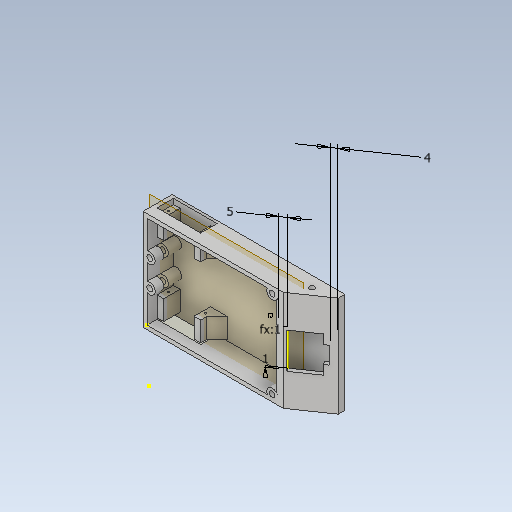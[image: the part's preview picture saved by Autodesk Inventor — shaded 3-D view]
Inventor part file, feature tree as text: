
AUTODESK INVENTOR PART (.ipt)
format: ipt  version: 2020 (Build 240168000, 168)  size: 331,776 bytes
history: native  units: mm
features: extrude x16, sketch x14, reference x11, other x8, projected_geometry x6, plane x2, hole x1, chamfer x1
ambient origin geometry x8: Origin, YZ Plane, XZ Plane, XY Plane, X Axis, Y Axis, Z Axis, Center Point
bodies: Solid1 (feature_tree)
feature tree (59):
  sketch  "Sketch1"  dims[d0=100.0mm d1=70.0mm]
  extrude  "Extrusion1"  Depth=70.0mm
  extrude  "Extrusion2"  Depth=2.0mm TaperAngle=0.0deg
  extrude  "Extrusion3"  Depth=33.0mm
  sketch  "Sketch3"  dims[d5=20.0mm d6=0.0mm d7=33.0mm]
  plane  "Work Plane1"
  extrude  "Extrusion4"  Depth=12.4mm TaperAngle=0.0deg
  hole  "Hole1"  [1 undecoded]
  sketch  "Sketch5"  dims[d11=15.0mm d12=15.0mm]
  extrude  "Extrusion5"  Depth=15.0mm
  extrude  "Extrusion6"  Depth=8.0mm
  extrude  "Extrusion7"  Depth=5.0mm TaperAngle=0.0deg
  extrude  "Extrusion8"  Depth=76.0mm TaperAngle=0.0deg
  extrude  "Extrusion9"  Depth=3.0mm TaperAngle=0.0deg
  extrude  "Extrusion10"  Depth=27.0mm
  sketch  "Sketch9"  dims[d33=5.0mm d40=41.25mm d41=0.0mm]
  sketch  "Sketch10"  dims[d42=3.0mm d43=76.0mm d44=0.0mm]
  extrude  "Extrusion12"  Depth=3.0mm
  sketch  "Sketch13"  dims[d49=21.75mm d50=0.0mm d52=27.0mm]
  extrude  "Extrusion13"  Depth=3.0mm TaperAngle=0.0deg
  extrude  "Extrusion14"  Depth=2.0mm
  sketch  "Sketch14"  dims[d53=20.0mm d54=3.0mm]
  extrude  "Extrusion15"  Depth=5.0mm
  extrude  "Extrusion16"  Depth=4.0mm
  plane  "Work Plane2"
  extrude  "Extrusion17"  Depth=1.0mm
  chamfer  "Chamfer1"  Distance=1.0mm
  sketch  "Sketch2"  dims[d2=3.0mm d3=2.0mm d4=0.0mm]
  reference  "Reference1"
  reference  "Reference2"
  reference  "Reference3"
  reference  "Reference4"
  reference  "Reference5"
  reference  "Reference6"
  reference  "Reference7"
  reference  "Reference8"
  sketch  "Sketch4"  dims[d8=12.4mm d9=30.0mm d10=0.0mm]
  reference  "Reference9"
  reference  "Reference10"
  sketch  "Sketch6"  dims[d13=15.0mm d14=15.0mm]
  sketch  "Sketch7"  dims[d15=30.0mm d16=0.0mm]
  projected_geometry  "Projected Loop1"
  sketch  "Sketch8"  dims[d17=1.5mm d18=6.0mm d19=4.0mm d20=2.0mm d21=90.0deg d22=8.0mm d23=0.0mm d32=30.0mm]
  projected_geometry  "Projected Loop2"
  sketch  "Sketch12"  dims[d45=3.0mm d46=0.0mm d47=3.0mm d48=0.0mm]
  reference  "Reference11"
  sketch  "Sketch15"  dims[d55=13.0mm d56=3.0mm d57=0.0mm d58=2.0mm d59=5.0mm d60=4.0mm d61=1.0mm d62=1.0mm d67=100.0mm d68=4.0mm d69=10.0mm d70=0.0mm d71=25.0mm d72=25.0mm d73=2.0mm d74=4.25mm d75=4.25mm d76=2.0mm d77=2.0mm d78=2.0mm d79=10.0mm d80=0.0mm d81=10.0mm d82=0.0mm d83=4.25mm d84=4.25mm d85=2.0mm d86=2.0mm d87=2.0mm d88=2.0mm d89=3.0mm d90=3.0mm d91=10.0mm d92=0.0mm d93=10.0mm d94=0.0mm d95=-10.0mm d96=3.5mm d97=0.0mm d98=8.0mm d99=2.0mm d100=45.0deg]
  projected_geometry  "Projected Loop4"
  projected_geometry  "Projected Loop5"
  projected_geometry  "Projected Loop6"
  projected_geometry  "Projected Loop7"
  other  "Assembly1"
  other  "Tower Pro MG90S Micro servo:2"
  other  "Крышка корпуса:1"
  other  "<userpath>\Desktop\3d\scanning-robot\Assembly1.iam"
  other  "Assembly1.iam"
  other  "Tower Pro MG90S Micro servo:1"
  other  "Цилиндрическое зубчатое зацепление:5"
  other  "Цилиндрическое зубчатое зацепление2:1"
note: 1 required parameter value undecoded (feature->parameter linkage not recoverable at this tier; creation-order binding heuristic only, values carry confidence <= 0.55)
